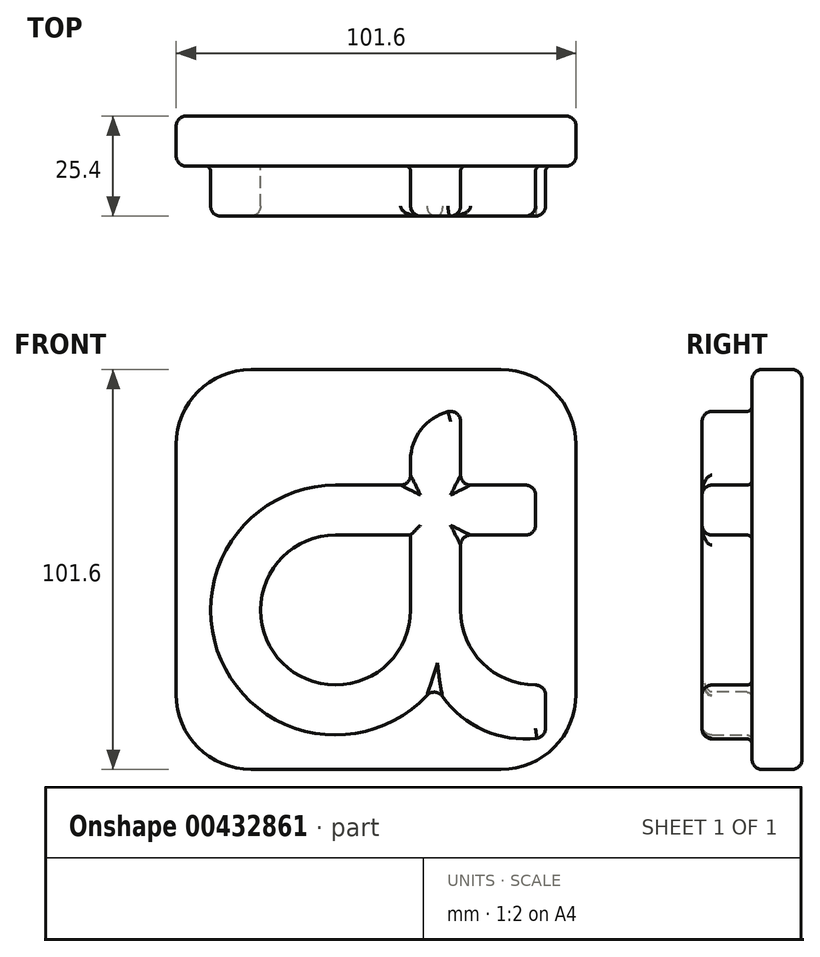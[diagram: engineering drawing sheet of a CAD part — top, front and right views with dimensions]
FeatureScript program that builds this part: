
annotation { "Feature Type Name" : "Feature", "Feature Type Description" : "" }
export const myFeature = defineFeature(function(context is Context, id is Id, definition is map)
    precondition{}
    {
        {
            var Q0;
            Q0=qCreatedBy(makeId("Front.planeOp"),FACE);
            var sketch = newSketch(context, id + "F0", { "sketchPlane" : qUnion([Q0])});
            skLineSegment(sketch, "E0.bottom", {"start": v(-31.75, 50.8) * mm, "end": v(31.75, 50.8) * mm});
            skLineSegment(sketch, "E0.top", {"start": v(-31.75, -50.8) * mm, "end": v(31.75, -50.8) * mm});
            skLineSegment(sketch, "E0.left", {"start": v(-50.8, 31.75) * mm, "end": v(-50.8, -31.75) * mm});
            skLineSegment(sketch, "E0.right", {"start": v(50.8, 31.75) * mm, "end": v(50.8, -31.75) * mm});
            skPoint(sketch, "E0.middle", {"position": v(0, 0) * mm});
            skPoint(sketch, "E1.visualSharp", {"position": v(-50.8, 50.8) * mm});
            skArc(sketch, "E1.filletArc", {"start": v(-31.75, 50.8) * mm, "mid": v(-45.22, 45.22) * mm, "end": v(-50.8, 31.75) * mm});
            skPoint(sketch, "E2.visualSharp", {"position": v(50.8, 50.8) * mm});
            skArc(sketch, "E2.filletArc", {"start": v(50.8, 31.75) * mm, "mid": v(45.22, 45.22) * mm, "end": v(31.75, 50.8) * mm});
            skPoint(sketch, "E3.visualSharp", {"position": v(50.8, -50.8) * mm});
            skArc(sketch, "E3.filletArc", {"start": v(31.75, -50.8) * mm, "mid": v(45.22, -45.22) * mm, "end": v(50.8, -31.75) * mm});
            skPoint(sketch, "E4.visualSharp", {"position": v(-50.8, -50.8) * mm});
            skArc(sketch, "E4.filletArc", {"start": v(-50.8, -31.75) * mm, "mid": v(-45.22, -45.22) * mm, "end": v(-31.75, -50.8) * mm});
            skArc(sketch, "E5", {"start": v(-10.3, 8.74) * mm, "mid": v(-23.78, -23.78) * mm, "end": v(8.74, -10.3) * mm});
            skLineSegment(sketch, "E6", {"start": v(-10.3, 8.74) * mm, "end": v(8.74, 8.74) * mm});
            skLineSegment(sketch, "E7", {"start": v(8.74, 8.74) * mm, "end": v(8.74, -10.3) * mm});
            skArc(sketch, "E8", {"start": v(-10.3, 21.44) * mm, "mid": v(-32.76, -32.76) * mm, "end": v(21.44, -10.3) * mm});
            skLineSegment(sketch, "E9", {"start": v(-10.3, 21.44) * mm, "end": v(21.44, 21.44) * mm});
            skLineSegment(sketch, "E10", {"start": v(21.44, 21.44) * mm, "end": v(21.44, -10.3) * mm});
            skLineSegment(sketch, "E11", {"start": v(8.74, -10.3) * mm, "end": v(21.44, -10.3) * mm, "construction": true});
            skLineSegment(sketch, "E12", {"start": v(-10.3, 8.74) * mm, "end": v(-10.3, 21.44) * mm, "construction": true});
            skLineSegment(sketch, "E13", {"start": v(8.74, 8.74) * mm, "end": v(0, 0) * mm, "construction": true});
            skLineSegment(sketch, "E14", {"start": v(21.44, 21.44) * mm, "end": v(21.44, 40.5) * mm});
            skLineSegment(sketch, "E15", {"start": v(8.74, 21.44) * mm, "end": v(8.74, 27.8) * mm});
            skArc(sketch, "E16", {"start": v(21.44, 40.5) * mm, "mid": v(12.46, 36.77) * mm, "end": v(8.74, 27.8) * mm});
            skArc(sketch, "E17", {"start": v(21.44, -10.3) * mm, "mid": v(27.95, -24.65) * mm, "end": v(43.03, -29.19) * mm});
            skLineSegment(sketch, "E18", {"start": v(-91.34, -29.36) * mm, "end": v(92.9, -29.36) * mm, "construction": true});
            skPoint(sketch, "E19", {"position": v(15.1, -29.36) * mm});
            skArc(sketch, "E20", {"start": v(15.1, -29.36) * mm, "mid": v(26.84, -40.65) * mm, "end": v(43.03, -42.48) * mm});
            skLineSegment(sketch, "E21", {"start": v(43.03, -29.19) * mm, "end": v(43.03, -42.48) * mm});
            skPoint(sketch, "E22", {"position": v(40.5, -29.36) * mm});
            skLineSegment(sketch, "E23", {"start": v(21.44, 21.44) * mm, "end": v(40.5, 21.44) * mm});
            skLineSegment(sketch, "E24", {"start": v(21.44, 8.74) * mm, "end": v(40.5, 8.74) * mm});
            skLineSegment(sketch, "E25", {"start": v(40.5, 8.74) * mm, "end": v(40.5, 21.44) * mm});
            skSolve(sketch);
        }
        {
            var Q0;
            Q0 = qSketchRegion(id + "F0", true);
            extrude(context, id + "F1", {"entities" : qUnion([Q0]), "depth" : 12.7 * mm});
        }
        {
            var Q0;
            Q0=makeQuery(id+"F0.imprint","IMPRINT",FACE,{"disambiguationData":[TD([[makeQuery(id+"F0.imprint","IMPRINT",EDGE,{"derivedFrom":sQuery(id+"F0.wireOp",EDGE,"E5")}),-1.0]])]});
            var Q1;
            {var subQ0=sQuery(id+"F0.wireOp",EDGE,"E23");Q1=makeQuery(id+"F0.imprint","IMPRINT",FACE,{"disambiguationData":[TD([[makeQuery(id+"F0.imprint","IMPRINT",EDGE,{"derivedFrom":subQ0}),-1.0]])]});}
            var Q2;
            {var subQ0=sQuery(id+"F0.wireOp",EDGE,"E17");Q2=makeQuery(id+"F0.imprint","IMPRINT",FACE,{"disambiguationData":[TD([[makeQuery(id+"F0.imprint","IMPRINT",EDGE,{"derivedFrom":subQ0}),-1.0]])]});}
            var Q3;
            {var subQ0=sQuery(id+"F0.wireOp",EDGE,"E14");Q3=makeQuery(id+"F0.imprint","IMPRINT",FACE,{"disambiguationData":[TD([[makeQuery(id+"F0.imprint","IMPRINT",EDGE,{"derivedFrom":subQ0}),1.0]])]});}
            extrude(context, id + "F2", {"entities" : qUnion([Q0, Q1, Q2, Q3]), "operationType" : NewBodyOperationType.ADD, "depth" : 25.4 * mm});
        }
        {
            var Q0;
            Q0=makeQuery(id+"F0.imprint","IMPRINT",FACE,{"disambiguationData":[TD([[makeQuery(id+"F0.imprint","IMPRINT",EDGE,{"derivedFrom":sQuery(id+"F0.wireOp",EDGE,"E5")}),1.0]])]});
            extrude(context, id + "F3", {"entities" : qUnion([Q0]), "operationType" : NewBodyOperationType.ADD, "depth" : 12.7 * mm});
        }
        {
            var Q0;
            Q0=makeQuery(id+"F1.opExtrude","CAP_EDGE",EDGE,{"disambiguationData":[OSD([sQuery(id+"F0.wireOp",EDGE,"E0.bottom")])],"isStart":false});
            var Q1;
            Q1=makeQuery(id+"F1.opExtrude","CAP_EDGE",EDGE,{"disambiguationData":[OSD([sQuery(id+"F0.wireOp",EDGE,"E1.filletArc")])],"isStart":false});
            var Q2;
            Q2=makeQuery(id+"F1.opExtrude","CAP_EDGE",EDGE,{"disambiguationData":[OSD([sQuery(id+"F0.wireOp",EDGE,"E0.left")])],"isStart":false});
            var Q3;
            Q3=makeQuery(id+"F1.opExtrude","CAP_EDGE",EDGE,{"disambiguationData":[OSD([sQuery(id+"F0.wireOp",EDGE,"E4.filletArc")])],"isStart":false});
            var Q4;
            Q4=makeQuery(id+"F1.opExtrude","CAP_EDGE",EDGE,{"disambiguationData":[OSD([sQuery(id+"F0.wireOp",EDGE,"E0.top")])],"isStart":false});
            var Q5;
            Q5=makeQuery(id+"F1.opExtrude","CAP_EDGE",EDGE,{"disambiguationData":[OSD([sQuery(id+"F0.wireOp",EDGE,"E3.filletArc")])],"isStart":false});
            var Q6;
            Q6=makeQuery(id+"F1.opExtrude","CAP_EDGE",EDGE,{"disambiguationData":[OSD([sQuery(id+"F0.wireOp",EDGE,"E0.right")])],"isStart":false});
            var Q7;
            Q7=makeQuery(id+"F1.opExtrude","CAP_EDGE",EDGE,{"disambiguationData":[OSD([sQuery(id+"F0.wireOp",EDGE,"E2.filletArc")])],"isStart":false});
            var Q8;
            Q8=makeQuery(id+"F1.opExtrude","CAP_EDGE",EDGE,{"disambiguationData":[OSD([sQuery(id+"F0.wireOp",EDGE,"E1.filletArc")])],"isStart":true});
            var Q9;
            Q9=makeQuery(id+"F1.opExtrude","CAP_EDGE",EDGE,{"disambiguationData":[OSD([sQuery(id+"F0.wireOp",EDGE,"E0.bottom")])],"isStart":true});
            var Q10;
            Q10=makeQuery(id+"F1.opExtrude","CAP_EDGE",EDGE,{"disambiguationData":[OSD([sQuery(id+"F0.wireOp",EDGE,"E2.filletArc")])],"isStart":true});
            var Q11;
            Q11=makeQuery(id+"F1.opExtrude","CAP_EDGE",EDGE,{"disambiguationData":[OSD([sQuery(id+"F0.wireOp",EDGE,"E0.right")])],"isStart":true});
            var Q12;
            Q12=makeQuery(id+"F1.opExtrude","CAP_EDGE",EDGE,{"disambiguationData":[OSD([sQuery(id+"F0.wireOp",EDGE,"E0.top")])],"isStart":true});
            var Q13;
            Q13=makeQuery(id+"F1.opExtrude","CAP_EDGE",EDGE,{"disambiguationData":[OSD([sQuery(id+"F0.wireOp",EDGE,"E3.filletArc")])],"isStart":true});
            var Q14;
            Q14=makeQuery(id+"F1.opExtrude","CAP_EDGE",EDGE,{"disambiguationData":[OSD([sQuery(id+"F0.wireOp",EDGE,"E4.filletArc")])],"isStart":true});
            var Q15;
            Q15=makeQuery(id+"F1.opExtrude","CAP_EDGE",EDGE,{"disambiguationData":[OSD([sQuery(id+"F0.wireOp",EDGE,"E0.left")])],"isStart":true});
            fillet(context, id + "F4", {"entities" : qUnion([Q0, Q1, Q2, Q3, Q4, Q5, Q6, Q7, Q8, Q9, Q10, Q11, Q12, Q13, Q14, Q15]), "radius" : 2.54 * mm, "tangentPropagation" : true, "allowEdgeOverflow" : false});
        }
        {
            var Q0;
            Q0=makeQuery(id+"F2.opExtrude","CAP_EDGE",EDGE,{"disambiguationData":[OSD([sQuery(id+"F0.wireOp",EDGE,"E9")])],"isStart":false});
            var Q1;
            Q1=makeQuery(id+"F2.opExtrude","CAP_EDGE",EDGE,{"disambiguationData":[OSD([sQuery(id+"F0.wireOp",EDGE,"E8")])],"isStart":false});
            var Q2;
            Q2=makeQuery(id+"F2.opExtrude","CAP_EDGE",EDGE,{"disambiguationData":[OSD([sQuery(id+"F0.wireOp",EDGE,"E6")])],"isStart":false});
            var Q3;
            Q3=makeQuery(id+"F2.opExtrude","CAP_EDGE",EDGE,{"disambiguationData":[OSD([sQuery(id+"F0.wireOp",EDGE,"E7")])],"isStart":false});
            var Q4;
            Q4=makeQuery(id+"F2.opExtrude","CAP_EDGE",EDGE,{"disambiguationData":[OSD([sQuery(id+"F0.wireOp",EDGE,"E5")])],"isStart":false});
            var Q5;
            Q5=makeQuery(id+"F2.opExtrude","CAP_EDGE",EDGE,{"disambiguationData":[OSD([sQuery(id+"F0.wireOp",EDGE,"E10")])],"isStart":false});
            var Q6;
            Q6=makeQuery(id+"F2.opExtrude","CAP_EDGE",EDGE,{"disambiguationData":[OSD([sQuery(id+"F0.wireOp",EDGE,"E24")])],"isStart":false});
            var Q7;
            Q7=makeQuery(id+"F2.opExtrude","CAP_EDGE",EDGE,{"disambiguationData":[OSD([sQuery(id+"F0.wireOp",EDGE,"E17")])],"isStart":false});
            var Q8;
            Q8=makeQuery(id+"F2.opExtrude","CAP_EDGE",EDGE,{"disambiguationData":[OSD([sQuery(id+"F0.wireOp",EDGE,"E20")])],"isStart":false});
            var Q9;
            Q9=makeQuery(id+"F2.opExtrude","CAP_EDGE",EDGE,{"disambiguationData":[OSD([sQuery(id+"F0.wireOp",EDGE,"E21")])],"isStart":false});
            var Q10;
            Q10=makeQuery(id+"F2.opExtrude","CAP_EDGE",EDGE,{"disambiguationData":[OSD([sQuery(id+"F0.wireOp",EDGE,"E14")])],"isStart":false});
            var Q11;
            Q11=makeQuery(id+"F2.opExtrude","CAP_EDGE",EDGE,{"disambiguationData":[OSD([sQuery(id+"F0.wireOp",EDGE,"E16")])],"isStart":false});
            var Q12;
            Q12=makeQuery(id+"F2.opExtrude","CAP_EDGE",EDGE,{"disambiguationData":[OSD([sQuery(id+"F0.wireOp",EDGE,"E15")])],"isStart":false});
            var Q13;
            Q13=makeQuery(id+"F2.opExtrude","CAP_EDGE",EDGE,{"disambiguationData":[OSD([sQuery(id+"F0.wireOp",EDGE,"E25")])],"isStart":false});
            var Q14;
            Q14=makeQuery(id+"F2.opExtrude","CAP_EDGE",EDGE,{"disambiguationData":[OSD([sQuery(id+"F0.wireOp",EDGE,"E23")])],"isStart":false});
            fillet(context, id + "F5", {"entities" : qUnion([Q0, Q1, Q2, Q3, Q4, Q5, Q6, Q7, Q8, Q9, Q10, Q11, Q12, Q13, Q14]), "radius" : 2.54 * mm, "tangentPropagation" : true, "allowEdgeOverflow" : false});
        }
        {
            var Q0;
            Q0=makeQuery(id+"F2.opExtrude","SWEPT_EDGE",EDGE,{"disambiguationData":[OSD([sQuery(id+"F0.wireOp",EDGE,"E9"),sQuery(id+"F0.wireOp",EDGE,"E10"),sQuery(id+"F0.wireOp",EDGE,"E14"),sQuery(id+"F0.wireOp",EDGE,"E23")])]});
            var Q1;
            Q1=makeQuery(id+"F2.opExtrude","SWEPT_EDGE",EDGE,{"disambiguationData":[OSD([sQuery(id+"F0.wireOp",EDGE,"E23"),sQuery(id+"F0.wireOp",EDGE,"E25")])]});
            var Q2;
            Q2=makeQuery(id+"F2.opExtrude","SWEPT_EDGE",EDGE,{"disambiguationData":[OSD([sQuery(id+"F0.wireOp",EDGE,"E24"),sQuery(id+"F0.wireOp",EDGE,"E25")])]});
            var Q3;
            Q3=makeQuery(id+"F2.opExtrude","SWEPT_EDGE",EDGE,{"disambiguationData":[OSD([sQuery(id+"F0.wireOp",EDGE,"E10"),sQuery(id+"F0.wireOp",EDGE,"E24")])]});
            var Q4;
            Q4=makeQuery(id+"F2.opExtrude","SWEPT_EDGE",EDGE,{"disambiguationData":[OSD([sQuery(id+"F0.wireOp",EDGE,"E8"),sQuery(id+"F0.wireOp",EDGE,"E10"),sQuery(id+"F0.wireOp",EDGE,"E17")])]});
            var Q5;
            Q5=makeQuery(id+"F2.opExtrude","SWEPT_EDGE",EDGE,{"disambiguationData":[OSD([sQuery(id+"F0.wireOp",EDGE,"E17"),sQuery(id+"F0.wireOp",EDGE,"E21")])]});
            var Q6;
            Q6=makeQuery(id+"F2.opExtrude","SWEPT_EDGE",EDGE,{"disambiguationData":[OSD([sQuery(id+"F0.wireOp",EDGE,"E20"),sQuery(id+"F0.wireOp",EDGE,"E21")])]});
            var Q7;
            Q7=makeQuery(id+"F2.opExtrude","SWEPT_EDGE",EDGE,{"disambiguationData":[OSD([sQuery(id+"F0.wireOp",EDGE,"E8"),sQuery(id+"F0.wireOp",EDGE,"E20")])]});
            var Q8;
            Q8=makeQuery(id+"F2.opExtrude","SWEPT_EDGE",EDGE,{"disambiguationData":[OSD([sQuery(id+"F0.wireOp",EDGE,"E9"),sQuery(id+"F0.wireOp",EDGE,"E15")])]});
            var Q9;
            Q9=makeQuery(id+"F2.opExtrude","SWEPT_EDGE",EDGE,{"disambiguationData":[OSD([sQuery(id+"F0.wireOp",EDGE,"E14"),sQuery(id+"F0.wireOp",EDGE,"E16")])]});
            fillet(context, id + "F6", {"entities" : qUnion([Q0, Q1, Q2, Q3, Q4, Q5, Q6, Q7, Q8, Q9]), "radius" : 2.54 * mm, "tangentPropagation" : true, "allowEdgeOverflow" : false});
        }
        {
            var Q0;
            Q0=makeQuery(id+"F1.opExtrude","CAP_EDGE",EDGE,{"disambiguationData":[OSD([sQuery(id+"F0.wireOp",EDGE,"E10")])],"isStart":false});
            var Q1;
            Q1=makeQuery(id+"F1.opExtrude","CAP_EDGE",EDGE,{"disambiguationData":[OSD([sQuery(id+"F0.wireOp",EDGE,"E17")])],"isStart":false});
            var Q2;
            {var subQ0=sQuery(id+"F0.wireOp",EDGE,"E24");var subQ1=sQuery(id+"F0.wireOp",EDGE,"E10");Q2=makeQuery(id+"F6.opFillet","BLEND_EDGE",EDGE,{"blendedFrom":[makeQuery(id+"F2.opExtrude","SWEPT_EDGE",EDGE,{"disambiguationData":[OSD([subQ1,subQ0])]}),makeQuery(id+"F1.opExtrude","CAP_FACE",FACE,{"disambiguationData":[OSD([sQuery(id+"F0.wireOp",EDGE,"E0.bottom"),sQuery(id+"F0.wireOp",EDGE,"E0.top"),sQuery(id+"F0.wireOp",EDGE,"E0.left"),sQuery(id+"F0.wireOp",EDGE,"E0.right"),sQuery(id+"F0.wireOp",EDGE,"E1.filletArc"),sQuery(id+"F0.wireOp",EDGE,"E2.filletArc"),sQuery(id+"F0.wireOp",EDGE,"E3.filletArc"),sQuery(id+"F0.wireOp",EDGE,"E4.filletArc"),sQuery(id+"F0.wireOp",EDGE,"E8"),sQuery(id+"F0.wireOp",EDGE,"E9"),subQ1,sQuery(id+"F0.wireOp",EDGE,"E14"),sQuery(id+"F0.wireOp",EDGE,"E15"),sQuery(id+"F0.wireOp",EDGE,"E16"),sQuery(id+"F0.wireOp",EDGE,"E17"),sQuery(id+"F0.wireOp",EDGE,"E20"),sQuery(id+"F0.wireOp",EDGE,"E21"),sQuery(id+"F0.wireOp",EDGE,"E23"),subQ0,sQuery(id+"F0.wireOp",EDGE,"E25")])],"isStart":false})],"blendedInto":[makeQuery(id+"F1.opExtrude","CAP_FACE",FACE,{"disambiguationData":[OSD([sQuery(id+"F0.wireOp",EDGE,"E0.bottom"),sQuery(id+"F0.wireOp",EDGE,"E0.top"),sQuery(id+"F0.wireOp",EDGE,"E0.left"),sQuery(id+"F0.wireOp",EDGE,"E0.right"),sQuery(id+"F0.wireOp",EDGE,"E1.filletArc"),sQuery(id+"F0.wireOp",EDGE,"E2.filletArc"),sQuery(id+"F0.wireOp",EDGE,"E3.filletArc"),sQuery(id+"F0.wireOp",EDGE,"E4.filletArc"),sQuery(id+"F0.wireOp",EDGE,"E8"),sQuery(id+"F0.wireOp",EDGE,"E9"),subQ1,sQuery(id+"F0.wireOp",EDGE,"E14"),sQuery(id+"F0.wireOp",EDGE,"E15"),sQuery(id+"F0.wireOp",EDGE,"E16"),sQuery(id+"F0.wireOp",EDGE,"E17"),sQuery(id+"F0.wireOp",EDGE,"E20"),sQuery(id+"F0.wireOp",EDGE,"E21"),sQuery(id+"F0.wireOp",EDGE,"E23"),subQ0,sQuery(id+"F0.wireOp",EDGE,"E25")])],"isStart":false})]});}
            var Q3;
            Q3=makeQuery(id+"F1.opExtrude","CAP_EDGE",EDGE,{"disambiguationData":[OSD([sQuery(id+"F0.wireOp",EDGE,"E24")])],"isStart":false});
            var Q4;
            {var subQ0=sQuery(id+"F0.wireOp",EDGE,"E25");var subQ1=sQuery(id+"F0.wireOp",EDGE,"E24");Q4=makeQuery(id+"F6.opFillet","BLEND_EDGE",EDGE,{"blendedFrom":[makeQuery(id+"F2.opExtrude","SWEPT_EDGE",EDGE,{"disambiguationData":[OSD([subQ1,subQ0])]}),makeQuery(id+"F1.opExtrude","CAP_FACE",FACE,{"disambiguationData":[OSD([sQuery(id+"F0.wireOp",EDGE,"E0.bottom"),sQuery(id+"F0.wireOp",EDGE,"E0.top"),sQuery(id+"F0.wireOp",EDGE,"E0.left"),sQuery(id+"F0.wireOp",EDGE,"E0.right"),sQuery(id+"F0.wireOp",EDGE,"E1.filletArc"),sQuery(id+"F0.wireOp",EDGE,"E2.filletArc"),sQuery(id+"F0.wireOp",EDGE,"E3.filletArc"),sQuery(id+"F0.wireOp",EDGE,"E4.filletArc"),sQuery(id+"F0.wireOp",EDGE,"E8"),sQuery(id+"F0.wireOp",EDGE,"E9"),sQuery(id+"F0.wireOp",EDGE,"E10"),sQuery(id+"F0.wireOp",EDGE,"E14"),sQuery(id+"F0.wireOp",EDGE,"E15"),sQuery(id+"F0.wireOp",EDGE,"E16"),sQuery(id+"F0.wireOp",EDGE,"E17"),sQuery(id+"F0.wireOp",EDGE,"E20"),sQuery(id+"F0.wireOp",EDGE,"E21"),sQuery(id+"F0.wireOp",EDGE,"E23"),subQ1,subQ0])],"isStart":false})],"blendedInto":[makeQuery(id+"F1.opExtrude","CAP_FACE",FACE,{"disambiguationData":[OSD([sQuery(id+"F0.wireOp",EDGE,"E0.bottom"),sQuery(id+"F0.wireOp",EDGE,"E0.top"),sQuery(id+"F0.wireOp",EDGE,"E0.left"),sQuery(id+"F0.wireOp",EDGE,"E0.right"),sQuery(id+"F0.wireOp",EDGE,"E1.filletArc"),sQuery(id+"F0.wireOp",EDGE,"E2.filletArc"),sQuery(id+"F0.wireOp",EDGE,"E3.filletArc"),sQuery(id+"F0.wireOp",EDGE,"E4.filletArc"),sQuery(id+"F0.wireOp",EDGE,"E8"),sQuery(id+"F0.wireOp",EDGE,"E9"),sQuery(id+"F0.wireOp",EDGE,"E10"),sQuery(id+"F0.wireOp",EDGE,"E14"),sQuery(id+"F0.wireOp",EDGE,"E15"),sQuery(id+"F0.wireOp",EDGE,"E16"),sQuery(id+"F0.wireOp",EDGE,"E17"),sQuery(id+"F0.wireOp",EDGE,"E20"),sQuery(id+"F0.wireOp",EDGE,"E21"),sQuery(id+"F0.wireOp",EDGE,"E23"),subQ1,subQ0])],"isStart":false})]});}
            var Q5;
            Q5=makeQuery(id+"F1.opExtrude","CAP_EDGE",EDGE,{"disambiguationData":[OSD([sQuery(id+"F0.wireOp",EDGE,"E25")])],"isStart":false});
            var Q6;
            {var subQ0=sQuery(id+"F0.wireOp",EDGE,"E21");var subQ1=sQuery(id+"F0.wireOp",EDGE,"E17");Q6=makeQuery(id+"F6.opFillet","BLEND_EDGE",EDGE,{"blendedFrom":[makeQuery(id+"F2.opExtrude","SWEPT_EDGE",EDGE,{"disambiguationData":[OSD([subQ1,subQ0])]}),makeQuery(id+"F1.opExtrude","CAP_FACE",FACE,{"disambiguationData":[OSD([sQuery(id+"F0.wireOp",EDGE,"E0.bottom"),sQuery(id+"F0.wireOp",EDGE,"E0.top"),sQuery(id+"F0.wireOp",EDGE,"E0.left"),sQuery(id+"F0.wireOp",EDGE,"E0.right"),sQuery(id+"F0.wireOp",EDGE,"E1.filletArc"),sQuery(id+"F0.wireOp",EDGE,"E2.filletArc"),sQuery(id+"F0.wireOp",EDGE,"E3.filletArc"),sQuery(id+"F0.wireOp",EDGE,"E4.filletArc"),sQuery(id+"F0.wireOp",EDGE,"E8"),sQuery(id+"F0.wireOp",EDGE,"E9"),sQuery(id+"F0.wireOp",EDGE,"E10"),sQuery(id+"F0.wireOp",EDGE,"E14"),sQuery(id+"F0.wireOp",EDGE,"E15"),sQuery(id+"F0.wireOp",EDGE,"E16"),subQ1,sQuery(id+"F0.wireOp",EDGE,"E20"),subQ0,sQuery(id+"F0.wireOp",EDGE,"E23"),sQuery(id+"F0.wireOp",EDGE,"E24"),sQuery(id+"F0.wireOp",EDGE,"E25")])],"isStart":false})],"blendedInto":[makeQuery(id+"F1.opExtrude","CAP_FACE",FACE,{"disambiguationData":[OSD([sQuery(id+"F0.wireOp",EDGE,"E0.bottom"),sQuery(id+"F0.wireOp",EDGE,"E0.top"),sQuery(id+"F0.wireOp",EDGE,"E0.left"),sQuery(id+"F0.wireOp",EDGE,"E0.right"),sQuery(id+"F0.wireOp",EDGE,"E1.filletArc"),sQuery(id+"F0.wireOp",EDGE,"E2.filletArc"),sQuery(id+"F0.wireOp",EDGE,"E3.filletArc"),sQuery(id+"F0.wireOp",EDGE,"E4.filletArc"),sQuery(id+"F0.wireOp",EDGE,"E8"),sQuery(id+"F0.wireOp",EDGE,"E9"),sQuery(id+"F0.wireOp",EDGE,"E10"),sQuery(id+"F0.wireOp",EDGE,"E14"),sQuery(id+"F0.wireOp",EDGE,"E15"),sQuery(id+"F0.wireOp",EDGE,"E16"),subQ1,sQuery(id+"F0.wireOp",EDGE,"E20"),subQ0,sQuery(id+"F0.wireOp",EDGE,"E23"),sQuery(id+"F0.wireOp",EDGE,"E24"),sQuery(id+"F0.wireOp",EDGE,"E25")])],"isStart":false})]});}
            var Q7;
            Q7=makeQuery(id+"F1.opExtrude","CAP_EDGE",EDGE,{"disambiguationData":[OSD([sQuery(id+"F0.wireOp",EDGE,"E21")])],"isStart":false});
            var Q8;
            Q8=makeQuery(id+"F1.opExtrude","CAP_EDGE",EDGE,{"disambiguationData":[OSD([sQuery(id+"F0.wireOp",EDGE,"E20")])],"isStart":false});
            var Q9;
            {var subQ0=sQuery(id+"F0.wireOp",EDGE,"E21");var subQ1=sQuery(id+"F0.wireOp",EDGE,"E20");Q9=makeQuery(id+"F6.opFillet","BLEND_EDGE",EDGE,{"blendedFrom":[makeQuery(id+"F2.opExtrude","SWEPT_EDGE",EDGE,{"disambiguationData":[OSD([subQ1,subQ0])]}),makeQuery(id+"F1.opExtrude","CAP_FACE",FACE,{"disambiguationData":[OSD([sQuery(id+"F0.wireOp",EDGE,"E0.bottom"),sQuery(id+"F0.wireOp",EDGE,"E0.top"),sQuery(id+"F0.wireOp",EDGE,"E0.left"),sQuery(id+"F0.wireOp",EDGE,"E0.right"),sQuery(id+"F0.wireOp",EDGE,"E1.filletArc"),sQuery(id+"F0.wireOp",EDGE,"E2.filletArc"),sQuery(id+"F0.wireOp",EDGE,"E3.filletArc"),sQuery(id+"F0.wireOp",EDGE,"E4.filletArc"),sQuery(id+"F0.wireOp",EDGE,"E8"),sQuery(id+"F0.wireOp",EDGE,"E9"),sQuery(id+"F0.wireOp",EDGE,"E10"),sQuery(id+"F0.wireOp",EDGE,"E14"),sQuery(id+"F0.wireOp",EDGE,"E15"),sQuery(id+"F0.wireOp",EDGE,"E16"),sQuery(id+"F0.wireOp",EDGE,"E17"),subQ1,subQ0,sQuery(id+"F0.wireOp",EDGE,"E23"),sQuery(id+"F0.wireOp",EDGE,"E24"),sQuery(id+"F0.wireOp",EDGE,"E25")])],"isStart":false})],"blendedInto":[makeQuery(id+"F1.opExtrude","CAP_FACE",FACE,{"disambiguationData":[OSD([sQuery(id+"F0.wireOp",EDGE,"E0.bottom"),sQuery(id+"F0.wireOp",EDGE,"E0.top"),sQuery(id+"F0.wireOp",EDGE,"E0.left"),sQuery(id+"F0.wireOp",EDGE,"E0.right"),sQuery(id+"F0.wireOp",EDGE,"E1.filletArc"),sQuery(id+"F0.wireOp",EDGE,"E2.filletArc"),sQuery(id+"F0.wireOp",EDGE,"E3.filletArc"),sQuery(id+"F0.wireOp",EDGE,"E4.filletArc"),sQuery(id+"F0.wireOp",EDGE,"E8"),sQuery(id+"F0.wireOp",EDGE,"E9"),sQuery(id+"F0.wireOp",EDGE,"E10"),sQuery(id+"F0.wireOp",EDGE,"E14"),sQuery(id+"F0.wireOp",EDGE,"E15"),sQuery(id+"F0.wireOp",EDGE,"E16"),sQuery(id+"F0.wireOp",EDGE,"E17"),subQ1,subQ0,sQuery(id+"F0.wireOp",EDGE,"E23"),sQuery(id+"F0.wireOp",EDGE,"E24"),sQuery(id+"F0.wireOp",EDGE,"E25")])],"isStart":false})]});}
            var Q10;
            {var subQ0=sQuery(id+"F0.wireOp",EDGE,"E20");var subQ1=sQuery(id+"F0.wireOp",EDGE,"E8");Q10=makeQuery(id+"F6.opFillet","BLEND_EDGE",EDGE,{"blendedFrom":[makeQuery(id+"F2.opExtrude","SWEPT_EDGE",EDGE,{"disambiguationData":[OSD([subQ1,subQ0])]}),makeQuery(id+"F1.opExtrude","CAP_FACE",FACE,{"disambiguationData":[OSD([sQuery(id+"F0.wireOp",EDGE,"E0.bottom"),sQuery(id+"F0.wireOp",EDGE,"E0.top"),sQuery(id+"F0.wireOp",EDGE,"E0.left"),sQuery(id+"F0.wireOp",EDGE,"E0.right"),sQuery(id+"F0.wireOp",EDGE,"E1.filletArc"),sQuery(id+"F0.wireOp",EDGE,"E2.filletArc"),sQuery(id+"F0.wireOp",EDGE,"E3.filletArc"),sQuery(id+"F0.wireOp",EDGE,"E4.filletArc"),subQ1,sQuery(id+"F0.wireOp",EDGE,"E9"),sQuery(id+"F0.wireOp",EDGE,"E10"),sQuery(id+"F0.wireOp",EDGE,"E14"),sQuery(id+"F0.wireOp",EDGE,"E15"),sQuery(id+"F0.wireOp",EDGE,"E16"),sQuery(id+"F0.wireOp",EDGE,"E17"),subQ0,sQuery(id+"F0.wireOp",EDGE,"E21"),sQuery(id+"F0.wireOp",EDGE,"E23"),sQuery(id+"F0.wireOp",EDGE,"E24"),sQuery(id+"F0.wireOp",EDGE,"E25")])],"isStart":false})],"blendedInto":[makeQuery(id+"F1.opExtrude","CAP_FACE",FACE,{"disambiguationData":[OSD([sQuery(id+"F0.wireOp",EDGE,"E0.bottom"),sQuery(id+"F0.wireOp",EDGE,"E0.top"),sQuery(id+"F0.wireOp",EDGE,"E0.left"),sQuery(id+"F0.wireOp",EDGE,"E0.right"),sQuery(id+"F0.wireOp",EDGE,"E1.filletArc"),sQuery(id+"F0.wireOp",EDGE,"E2.filletArc"),sQuery(id+"F0.wireOp",EDGE,"E3.filletArc"),sQuery(id+"F0.wireOp",EDGE,"E4.filletArc"),subQ1,sQuery(id+"F0.wireOp",EDGE,"E9"),sQuery(id+"F0.wireOp",EDGE,"E10"),sQuery(id+"F0.wireOp",EDGE,"E14"),sQuery(id+"F0.wireOp",EDGE,"E15"),sQuery(id+"F0.wireOp",EDGE,"E16"),sQuery(id+"F0.wireOp",EDGE,"E17"),subQ0,sQuery(id+"F0.wireOp",EDGE,"E21"),sQuery(id+"F0.wireOp",EDGE,"E23"),sQuery(id+"F0.wireOp",EDGE,"E24"),sQuery(id+"F0.wireOp",EDGE,"E25")])],"isStart":false})]});}
            var Q11;
            Q11=makeQuery(id+"F1.opExtrude","CAP_EDGE",EDGE,{"disambiguationData":[OSD([sQuery(id+"F0.wireOp",EDGE,"E8")])],"isStart":false});
            var Q12;
            Q12=makeQuery(id+"F1.opExtrude","CAP_EDGE",EDGE,{"disambiguationData":[OSD([sQuery(id+"F0.wireOp",EDGE,"E9")])],"isStart":false});
            var Q13;
            {var subQ0=sQuery(id+"F0.wireOp",EDGE,"E15");var subQ1=sQuery(id+"F0.wireOp",EDGE,"E9");Q13=makeQuery(id+"F6.opFillet","BLEND_EDGE",EDGE,{"blendedFrom":[makeQuery(id+"F2.opExtrude","SWEPT_EDGE",EDGE,{"disambiguationData":[OSD([subQ1,subQ0])]}),makeQuery(id+"F1.opExtrude","CAP_FACE",FACE,{"disambiguationData":[OSD([sQuery(id+"F0.wireOp",EDGE,"E0.bottom"),sQuery(id+"F0.wireOp",EDGE,"E0.top"),sQuery(id+"F0.wireOp",EDGE,"E0.left"),sQuery(id+"F0.wireOp",EDGE,"E0.right"),sQuery(id+"F0.wireOp",EDGE,"E1.filletArc"),sQuery(id+"F0.wireOp",EDGE,"E2.filletArc"),sQuery(id+"F0.wireOp",EDGE,"E3.filletArc"),sQuery(id+"F0.wireOp",EDGE,"E4.filletArc"),sQuery(id+"F0.wireOp",EDGE,"E8"),subQ1,sQuery(id+"F0.wireOp",EDGE,"E10"),sQuery(id+"F0.wireOp",EDGE,"E14"),subQ0,sQuery(id+"F0.wireOp",EDGE,"E16"),sQuery(id+"F0.wireOp",EDGE,"E17"),sQuery(id+"F0.wireOp",EDGE,"E20"),sQuery(id+"F0.wireOp",EDGE,"E21"),sQuery(id+"F0.wireOp",EDGE,"E23"),sQuery(id+"F0.wireOp",EDGE,"E24"),sQuery(id+"F0.wireOp",EDGE,"E25")])],"isStart":false})],"blendedInto":[makeQuery(id+"F1.opExtrude","CAP_FACE",FACE,{"disambiguationData":[OSD([sQuery(id+"F0.wireOp",EDGE,"E0.bottom"),sQuery(id+"F0.wireOp",EDGE,"E0.top"),sQuery(id+"F0.wireOp",EDGE,"E0.left"),sQuery(id+"F0.wireOp",EDGE,"E0.right"),sQuery(id+"F0.wireOp",EDGE,"E1.filletArc"),sQuery(id+"F0.wireOp",EDGE,"E2.filletArc"),sQuery(id+"F0.wireOp",EDGE,"E3.filletArc"),sQuery(id+"F0.wireOp",EDGE,"E4.filletArc"),sQuery(id+"F0.wireOp",EDGE,"E8"),subQ1,sQuery(id+"F0.wireOp",EDGE,"E10"),sQuery(id+"F0.wireOp",EDGE,"E14"),subQ0,sQuery(id+"F0.wireOp",EDGE,"E16"),sQuery(id+"F0.wireOp",EDGE,"E17"),sQuery(id+"F0.wireOp",EDGE,"E20"),sQuery(id+"F0.wireOp",EDGE,"E21"),sQuery(id+"F0.wireOp",EDGE,"E23"),sQuery(id+"F0.wireOp",EDGE,"E24"),sQuery(id+"F0.wireOp",EDGE,"E25")])],"isStart":false})]});}
            var Q14;
            Q14=makeQuery(id+"F1.opExtrude","CAP_EDGE",EDGE,{"disambiguationData":[OSD([sQuery(id+"F0.wireOp",EDGE,"E15")])],"isStart":false});
            var Q15;
            Q15=makeQuery(id+"F1.opExtrude","CAP_EDGE",EDGE,{"disambiguationData":[OSD([sQuery(id+"F0.wireOp",EDGE,"E16")])],"isStart":false});
            var Q16;
            Q16=makeQuery(id+"F1.opExtrude","CAP_EDGE",EDGE,{"disambiguationData":[OSD([sQuery(id+"F0.wireOp",EDGE,"E14")])],"isStart":false});
            var Q17;
            {var subQ0=sQuery(id+"F0.wireOp",EDGE,"E16");var subQ1=sQuery(id+"F0.wireOp",EDGE,"E14");Q17=makeQuery(id+"F6.opFillet","BLEND_EDGE",EDGE,{"blendedFrom":[makeQuery(id+"F2.opExtrude","SWEPT_EDGE",EDGE,{"disambiguationData":[OSD([subQ1,subQ0])]}),makeQuery(id+"F1.opExtrude","CAP_FACE",FACE,{"disambiguationData":[OSD([sQuery(id+"F0.wireOp",EDGE,"E0.bottom"),sQuery(id+"F0.wireOp",EDGE,"E0.top"),sQuery(id+"F0.wireOp",EDGE,"E0.left"),sQuery(id+"F0.wireOp",EDGE,"E0.right"),sQuery(id+"F0.wireOp",EDGE,"E1.filletArc"),sQuery(id+"F0.wireOp",EDGE,"E2.filletArc"),sQuery(id+"F0.wireOp",EDGE,"E3.filletArc"),sQuery(id+"F0.wireOp",EDGE,"E4.filletArc"),sQuery(id+"F0.wireOp",EDGE,"E8"),sQuery(id+"F0.wireOp",EDGE,"E9"),sQuery(id+"F0.wireOp",EDGE,"E10"),subQ1,sQuery(id+"F0.wireOp",EDGE,"E15"),subQ0,sQuery(id+"F0.wireOp",EDGE,"E17"),sQuery(id+"F0.wireOp",EDGE,"E20"),sQuery(id+"F0.wireOp",EDGE,"E21"),sQuery(id+"F0.wireOp",EDGE,"E23"),sQuery(id+"F0.wireOp",EDGE,"E24"),sQuery(id+"F0.wireOp",EDGE,"E25")])],"isStart":false})],"blendedInto":[makeQuery(id+"F1.opExtrude","CAP_FACE",FACE,{"disambiguationData":[OSD([sQuery(id+"F0.wireOp",EDGE,"E0.bottom"),sQuery(id+"F0.wireOp",EDGE,"E0.top"),sQuery(id+"F0.wireOp",EDGE,"E0.left"),sQuery(id+"F0.wireOp",EDGE,"E0.right"),sQuery(id+"F0.wireOp",EDGE,"E1.filletArc"),sQuery(id+"F0.wireOp",EDGE,"E2.filletArc"),sQuery(id+"F0.wireOp",EDGE,"E3.filletArc"),sQuery(id+"F0.wireOp",EDGE,"E4.filletArc"),sQuery(id+"F0.wireOp",EDGE,"E8"),sQuery(id+"F0.wireOp",EDGE,"E9"),sQuery(id+"F0.wireOp",EDGE,"E10"),subQ1,sQuery(id+"F0.wireOp",EDGE,"E15"),subQ0,sQuery(id+"F0.wireOp",EDGE,"E17"),sQuery(id+"F0.wireOp",EDGE,"E20"),sQuery(id+"F0.wireOp",EDGE,"E21"),sQuery(id+"F0.wireOp",EDGE,"E23"),sQuery(id+"F0.wireOp",EDGE,"E24"),sQuery(id+"F0.wireOp",EDGE,"E25")])],"isStart":false})]});}
            var Q18;
            {var subQ0=sQuery(id+"F0.wireOp",EDGE,"E23");var subQ1=sQuery(id+"F0.wireOp",EDGE,"E14");var subQ2=sQuery(id+"F0.wireOp",EDGE,"E10");var subQ3=sQuery(id+"F0.wireOp",EDGE,"E9");Q18=makeQuery(id+"F6.opFillet","BLEND_EDGE",EDGE,{"blendedFrom":[makeQuery(id+"F2.opExtrude","SWEPT_EDGE",EDGE,{"disambiguationData":[OSD([subQ3,subQ2,subQ1,subQ0])]}),makeQuery(id+"F1.opExtrude","CAP_FACE",FACE,{"disambiguationData":[OSD([sQuery(id+"F0.wireOp",EDGE,"E0.bottom"),sQuery(id+"F0.wireOp",EDGE,"E0.top"),sQuery(id+"F0.wireOp",EDGE,"E0.left"),sQuery(id+"F0.wireOp",EDGE,"E0.right"),sQuery(id+"F0.wireOp",EDGE,"E1.filletArc"),sQuery(id+"F0.wireOp",EDGE,"E2.filletArc"),sQuery(id+"F0.wireOp",EDGE,"E3.filletArc"),sQuery(id+"F0.wireOp",EDGE,"E4.filletArc"),sQuery(id+"F0.wireOp",EDGE,"E8"),subQ3,subQ2,subQ1,sQuery(id+"F0.wireOp",EDGE,"E15"),sQuery(id+"F0.wireOp",EDGE,"E16"),sQuery(id+"F0.wireOp",EDGE,"E17"),sQuery(id+"F0.wireOp",EDGE,"E20"),sQuery(id+"F0.wireOp",EDGE,"E21"),subQ0,sQuery(id+"F0.wireOp",EDGE,"E24"),sQuery(id+"F0.wireOp",EDGE,"E25")])],"isStart":false})],"blendedInto":[makeQuery(id+"F1.opExtrude","CAP_FACE",FACE,{"disambiguationData":[OSD([sQuery(id+"F0.wireOp",EDGE,"E0.bottom"),sQuery(id+"F0.wireOp",EDGE,"E0.top"),sQuery(id+"F0.wireOp",EDGE,"E0.left"),sQuery(id+"F0.wireOp",EDGE,"E0.right"),sQuery(id+"F0.wireOp",EDGE,"E1.filletArc"),sQuery(id+"F0.wireOp",EDGE,"E2.filletArc"),sQuery(id+"F0.wireOp",EDGE,"E3.filletArc"),sQuery(id+"F0.wireOp",EDGE,"E4.filletArc"),sQuery(id+"F0.wireOp",EDGE,"E8"),subQ3,subQ2,subQ1,sQuery(id+"F0.wireOp",EDGE,"E15"),sQuery(id+"F0.wireOp",EDGE,"E16"),sQuery(id+"F0.wireOp",EDGE,"E17"),sQuery(id+"F0.wireOp",EDGE,"E20"),sQuery(id+"F0.wireOp",EDGE,"E21"),subQ0,sQuery(id+"F0.wireOp",EDGE,"E24"),sQuery(id+"F0.wireOp",EDGE,"E25")])],"isStart":false})]});}
            var Q19;
            Q19=makeQuery(id+"F1.opExtrude","CAP_EDGE",EDGE,{"disambiguationData":[OSD([sQuery(id+"F0.wireOp",EDGE,"E23")])],"isStart":false});
            var Q20;
            {var subQ0=sQuery(id+"F0.wireOp",EDGE,"E25");var subQ1=sQuery(id+"F0.wireOp",EDGE,"E23");Q20=makeQuery(id+"F6.opFillet","BLEND_EDGE",EDGE,{"blendedFrom":[makeQuery(id+"F2.opExtrude","SWEPT_EDGE",EDGE,{"disambiguationData":[OSD([subQ1,subQ0])]}),makeQuery(id+"F1.opExtrude","CAP_FACE",FACE,{"disambiguationData":[OSD([sQuery(id+"F0.wireOp",EDGE,"E0.bottom"),sQuery(id+"F0.wireOp",EDGE,"E0.top"),sQuery(id+"F0.wireOp",EDGE,"E0.left"),sQuery(id+"F0.wireOp",EDGE,"E0.right"),sQuery(id+"F0.wireOp",EDGE,"E1.filletArc"),sQuery(id+"F0.wireOp",EDGE,"E2.filletArc"),sQuery(id+"F0.wireOp",EDGE,"E3.filletArc"),sQuery(id+"F0.wireOp",EDGE,"E4.filletArc"),sQuery(id+"F0.wireOp",EDGE,"E8"),sQuery(id+"F0.wireOp",EDGE,"E9"),sQuery(id+"F0.wireOp",EDGE,"E10"),sQuery(id+"F0.wireOp",EDGE,"E14"),sQuery(id+"F0.wireOp",EDGE,"E15"),sQuery(id+"F0.wireOp",EDGE,"E16"),sQuery(id+"F0.wireOp",EDGE,"E17"),sQuery(id+"F0.wireOp",EDGE,"E20"),sQuery(id+"F0.wireOp",EDGE,"E21"),subQ1,sQuery(id+"F0.wireOp",EDGE,"E24"),subQ0])],"isStart":false})],"blendedInto":[makeQuery(id+"F1.opExtrude","CAP_FACE",FACE,{"disambiguationData":[OSD([sQuery(id+"F0.wireOp",EDGE,"E0.bottom"),sQuery(id+"F0.wireOp",EDGE,"E0.top"),sQuery(id+"F0.wireOp",EDGE,"E0.left"),sQuery(id+"F0.wireOp",EDGE,"E0.right"),sQuery(id+"F0.wireOp",EDGE,"E1.filletArc"),sQuery(id+"F0.wireOp",EDGE,"E2.filletArc"),sQuery(id+"F0.wireOp",EDGE,"E3.filletArc"),sQuery(id+"F0.wireOp",EDGE,"E4.filletArc"),sQuery(id+"F0.wireOp",EDGE,"E8"),sQuery(id+"F0.wireOp",EDGE,"E9"),sQuery(id+"F0.wireOp",EDGE,"E10"),sQuery(id+"F0.wireOp",EDGE,"E14"),sQuery(id+"F0.wireOp",EDGE,"E15"),sQuery(id+"F0.wireOp",EDGE,"E16"),sQuery(id+"F0.wireOp",EDGE,"E17"),sQuery(id+"F0.wireOp",EDGE,"E20"),sQuery(id+"F0.wireOp",EDGE,"E21"),subQ1,sQuery(id+"F0.wireOp",EDGE,"E24"),subQ0])],"isStart":false})]});}
            var Q21;
            Q21=makeQuery(id+"F3.opExtrude","CAP_EDGE",EDGE,{"disambiguationData":[OSD([sQuery(id+"F0.wireOp",EDGE,"E5")])],"isStart":false});
            var Q22;
            Q22=makeQuery(id+"F3.opExtrude","CAP_EDGE",EDGE,{"disambiguationData":[OSD([sQuery(id+"F0.wireOp",EDGE,"E6")])],"isStart":false});
            var Q23;
            Q23=makeQuery(id+"F3.opExtrude","CAP_EDGE",EDGE,{"disambiguationData":[OSD([sQuery(id+"F0.wireOp",EDGE,"E7")])],"isStart":false});
            fillet(context, id + "F7", {"entities" : qUnion([Q0, Q1, Q2, Q3, Q4, Q5, Q6, Q7, Q8, Q9, Q10, Q11, Q12, Q13, Q14, Q15, Q16, Q17, Q18, Q19, Q20, Q21, Q22, Q23]), "radius" : 1.27 * mm, "tangentPropagation" : true, "allowEdgeOverflow" : false});
        }
    });
